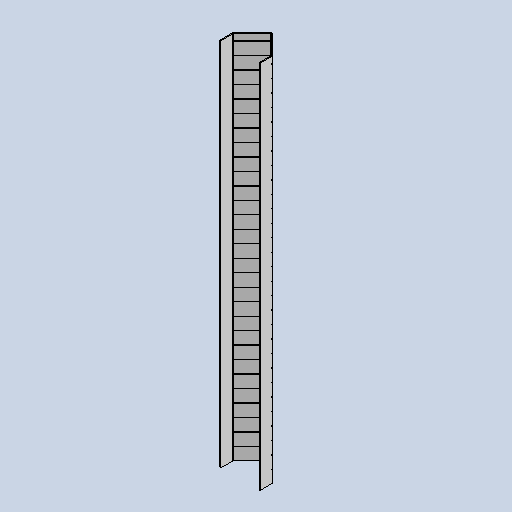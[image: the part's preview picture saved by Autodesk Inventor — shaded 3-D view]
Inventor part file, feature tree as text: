
AUTODESK INVENTOR PART (.ipt)
format: ipt  version: 2025.3 (Build 293356030, 356C)  size: 890,880 bytes
history: native  units: mm
features: sheet_metal_op x3, sketch x3, other x3, mirror x1
ambient origin geometry x8: Origin, YZ Plane, XZ Plane, XY Plane, X Axis, Y Axis, Z Axis, Center Point
bodies: Body1 (feature_tree)
feature tree (10):
  sheet_metal_op  "Contour Flange1"
  mirror  "Mirror2"
  sketch  "Sketch3"  dims[d15=10.0mm]
  other  "Plate1"
  sheet_metal_op  "Bend1"
  sheet_metal_op  "Corner1"
  sketch  "Sketch5"  dims[d19=1.0mm d20=1.0mm d21=0.8mm d22=0.8mm d23=0.4mm d24=1.6mm d25=0.8mm d26=295.0mm d27=0.8mm d28=0.8mm d29=3.2mm d30=0.8mm d31=0.8mm d32=32.0mm d33=90.0deg d111=0.2mm d112=28.0mm d113=5.0mm d114=0.5mm d115=290.0mm d116=10.0mm d73=10.0mm d75=10.0mm d97=5.0mm d98=0.8mm d99=0.0mm d101=0.5mm d102=0.872665mm d103=0.5mm d104=0.872665mm]
  sketch  "Sketch Rectangular Pattern3"  dims[d18=1.0mm]
  other  "Cut3"
  other  "Definition1"
